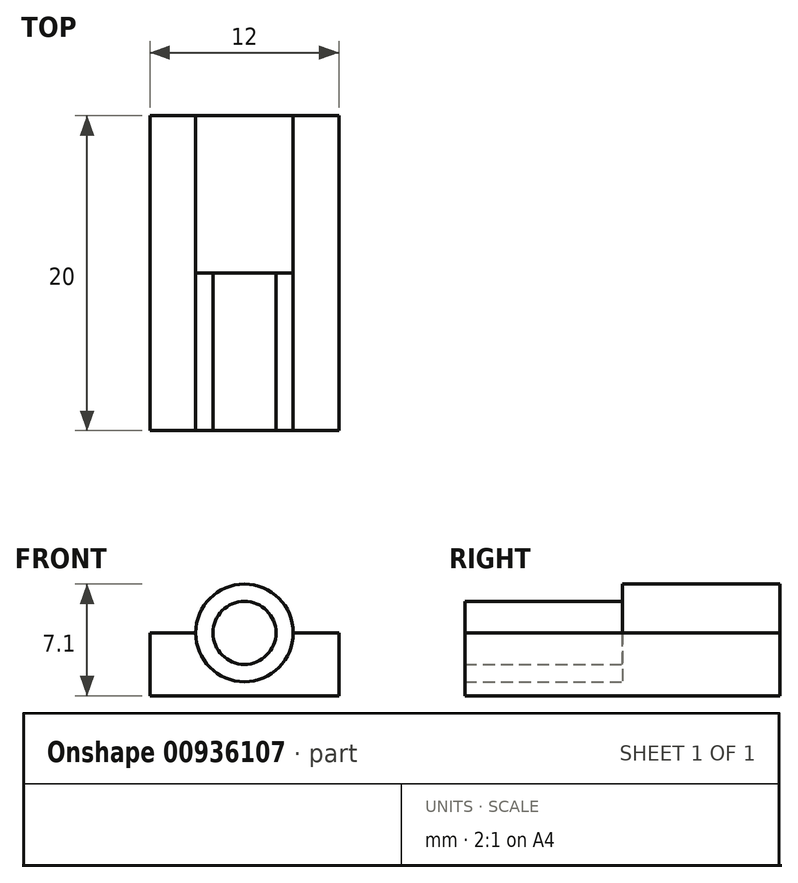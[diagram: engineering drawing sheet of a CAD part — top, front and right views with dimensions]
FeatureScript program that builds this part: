
annotation { "Feature Type Name" : "Feature", "Feature Type Description" : "" }
export const myFeature = defineFeature(function(context is Context, id is Id, definition is map)
    precondition{}
    {
        {
            var Q0;
            Q0=qCreatedBy(makeId("Front.planeOp"),FACE);
            var sketch = newSketch(context, id + "F0", { "sketchPlane" : qUnion([Q0])});
            skCircle(sketch, "E0", {"center": v(0, 0) * mm, "radius": 2 * mm});
            skCircle(sketch, "E1", {"center": v(0, 0) * mm, "radius": 3.1 * mm});
            skLineSegment(sketch, "E2.bottom", {"start": v(-6, 0) * mm, "end": v(6, 0) * mm});
            skLineSegment(sketch, "E2.top", {"start": v(-6, -4) * mm, "end": v(6, -4) * mm});
            skLineSegment(sketch, "E2.left", {"start": v(-6, 0) * mm, "end": v(-6, -4) * mm});
            skLineSegment(sketch, "E2.right", {"start": v(6, 0) * mm, "end": v(6, -4) * mm});
            skSolve(sketch);
        }
        {
            var Q0;
            {var subQ0=sQuery(id+"F0.wireOp",EDGE,"E2.bottom");var subQ1=sQuery(id+"F0.wireOp",EDGE,"E0");var subQ2=makeQuery(id+"F0.imprint","INTERSECT",VERTEX,{"disambiguationData":[OD(0.0)],"derivedFrom":[subQ1,subQ0]});Q0=makeQuery(id+"F0.imprint","IMPRINT",FACE,{"disambiguationData":[TD([[makeQuery(id+"F0.imprint","IMPRINT",EDGE,{"disambiguationData":[TD([[subQ2,1.0]])],"derivedFrom":subQ1}),-1.0]])]});}
            var Q1;
            {var subQ0=sQuery(id+"F0.wireOp",EDGE,"E2.bottom");var subQ1=sQuery(id+"F0.wireOp",EDGE,"E0");var subQ2=makeQuery(id+"F0.imprint","INTERSECT",VERTEX,{"disambiguationData":[OD(0.0)],"derivedFrom":[subQ1,subQ0]});Q1=makeQuery(id+"F0.imprint","IMPRINT",FACE,{"disambiguationData":[TD([[makeQuery(id+"F0.imprint","IMPRINT",EDGE,{"disambiguationData":[TD([[subQ2,-1.0]])],"derivedFrom":subQ1}),-1.0]])]});}
            extrude(context, id + "F1", {"entities" : qUnion([Q0, Q1]), "depth" : 10 * mm, "offsetDistance" : 25 * mm});
        }
        {
            var Q0;
            Q0=makeQuery(id+"F0.imprint","IMPRINT",FACE,{"disambiguationData":[TD([[makeQuery(id+"F0.imprint","IMPRINT",EDGE,{"derivedFrom":sQuery(id+"F0.wireOp",EDGE,"E2.top")}),1.0]])]});
            var Q1;
            {var subQ0=sQuery(id+"F0.wireOp",EDGE,"E2.bottom");var subQ1=sQuery(id+"F0.wireOp",EDGE,"E0");var subQ2=makeQuery(id+"F0.imprint","INTERSECT",VERTEX,{"disambiguationData":[OD(0.0)],"derivedFrom":[subQ1,subQ0]});Q1=makeQuery(id+"F0.imprint","IMPRINT",FACE,{"disambiguationData":[TD([[makeQuery(id+"F0.imprint","IMPRINT",EDGE,{"disambiguationData":[TD([[subQ2,1.0]])],"derivedFrom":subQ1}),1.0]])]});}
            var Q2;
            {var subQ0=sQuery(id+"F0.wireOp",EDGE,"E2.bottom");var subQ1=sQuery(id+"F0.wireOp",EDGE,"E0");var subQ2=makeQuery(id+"F0.imprint","INTERSECT",VERTEX,{"disambiguationData":[OD(0.0)],"derivedFrom":[subQ1,subQ0]});Q2=makeQuery(id+"F0.imprint","IMPRINT",FACE,{"disambiguationData":[TD([[makeQuery(id+"F0.imprint","IMPRINT",EDGE,{"disambiguationData":[TD([[subQ2,-1.0]])],"derivedFrom":subQ1}),1.0]])]});}
            extrude(context, id + "F2", {"entities" : qUnion([Q0, Q1, Q2]), "operationType" : NewBodyOperationType.ADD, "depth" : 20 * mm, "offsetDistance" : 25 * mm});
        }
        {
            var Q0;
            Q0=makeQuery(id+"F2.opExtrude","CAP_FACE",FACE,{"disambiguationData":[OSD([sQuery(id+"F0.wireOp",EDGE,"E1"),sQuery(id+"F0.wireOp",EDGE,"E2.bottom"),sQuery(id+"F0.wireOp",EDGE,"E2.top"),sQuery(id+"F0.wireOp",EDGE,"E2.left"),sQuery(id+"F0.wireOp",EDGE,"E2.right")])],"isStart":false});
            cPlane(context, id + "F3", {"entities" : qUnion([Q0]), "cplaneType" : CPlaneType.OFFSET, "offset" : 0 * mm, "width" : 150 * mm, "height" : 150 * mm});
        }
    });
